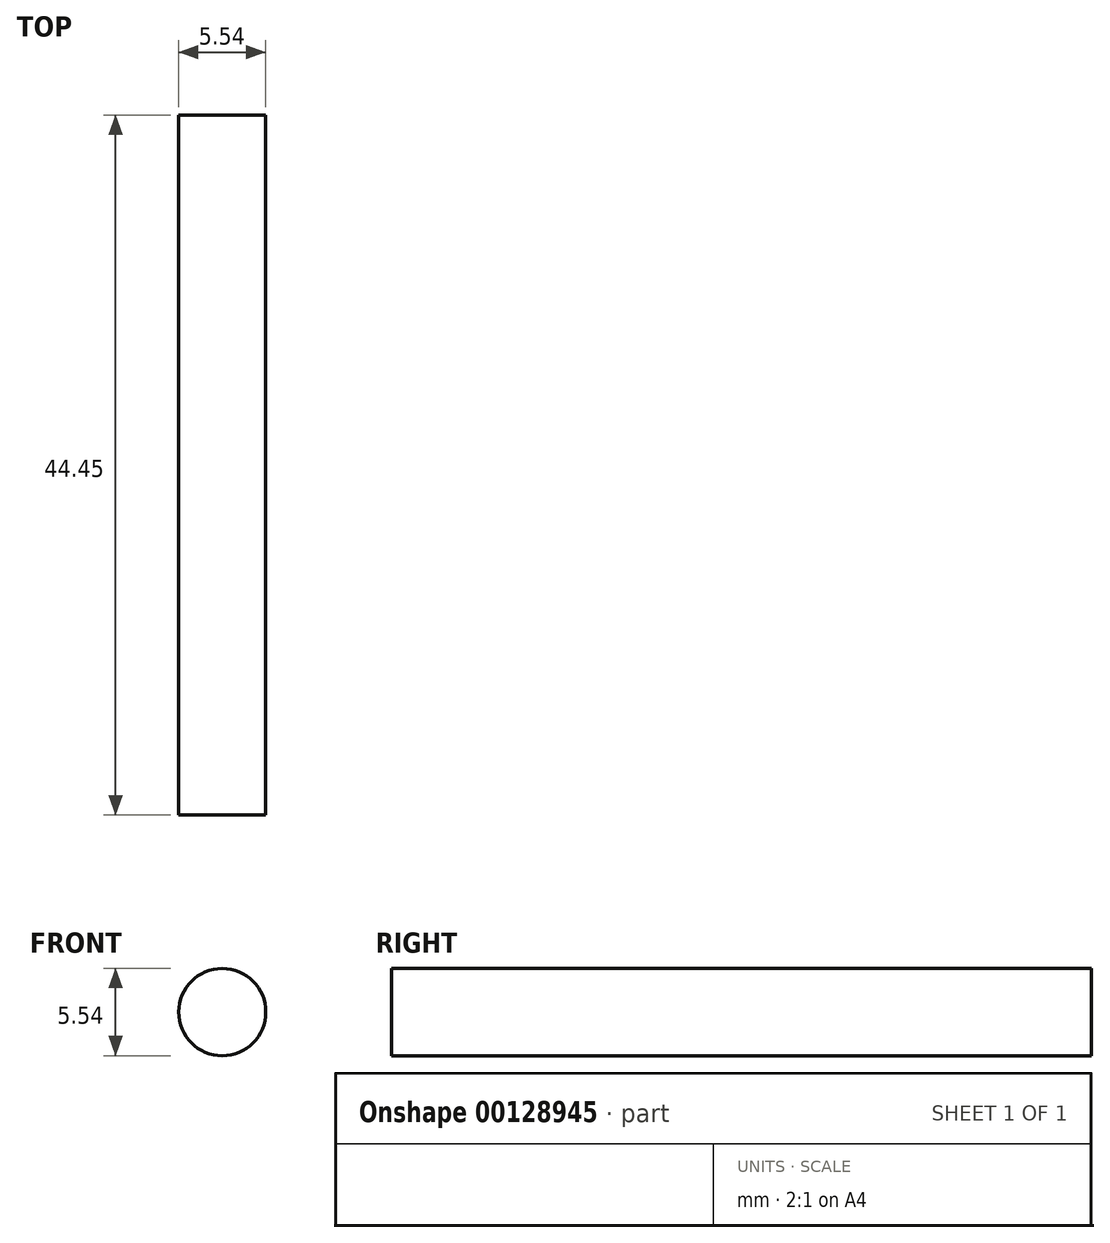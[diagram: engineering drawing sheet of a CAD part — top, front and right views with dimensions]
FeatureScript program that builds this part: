
annotation { "Feature Type Name" : "Feature", "Feature Type Description" : "" }
export const myFeature = defineFeature(function(context is Context, id is Id, definition is map)
    precondition{}
    {
        {
            var Q0;
            Q0=qCreatedBy(makeId("Front.planeOp"),FACE);
            var sketch = newSketch(context, id + "F0", { "sketchPlane" : qUnion([Q0])});
            skCircle(sketch, "E0", {"center": v(0, 0) * mm, "radius": 2.77 * mm});
            skSolve(sketch);
        }
        {
            var Q0;
            Q0=makeQuery(id+"F0.imprint","IMPRINT",FACE,{"disambiguationData":[TD([[makeQuery(id+"F0.imprint","IMPRINT",EDGE,{"derivedFrom":sQuery(id+"F0.wireOp",EDGE,"E0")}),1.0]])]});
            extrude(context, id + "F1", {"entities" : qUnion([Q0]), "depth" : 44.45 * mm});
        }
    });
